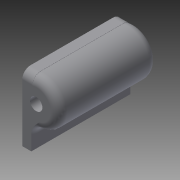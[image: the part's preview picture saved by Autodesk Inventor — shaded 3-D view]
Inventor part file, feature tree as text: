
AUTODESK INVENTOR PART (.ipt)
format: ipt  version: 2015 (Build 190159000, 159)  size: 192,000 bytes
history: native  units: in
note: dims shown in document units (in); Inventor stores cm internally (conversion verified against a paired STEP export)
features: fillet x3, extrude x2, sketch x2
ambient origin geometry x8: Origin, YZ Plane, XZ Plane, XY Plane, X Axis, Y Axis, Z Axis, Center Point
bodies: Solid1 (feature_tree)
feature tree (7):
  extrude  "Extrusion1"  Depth=0.1875in
  extrude  "Extrusion2"  Depth=0.125in
  fillet  "Fillet2"  Radius=0.1094in
  fillet  "Fillet3"  Radius=1.5in
  fillet  "Fillet4"  Radius=0.25in
  sketch  "Sketch1"  dims[d1=0.1482in d2=1.0in d3=0.1875in]
  sketch  "Sketch2"  dims[d4=1.5in d5=0.0in d6=0.1094in d7=0.1094in d8=1.5in d9=0.0in d11=0.25in d12=0.125in d13=0.125in d14=0.125in]
